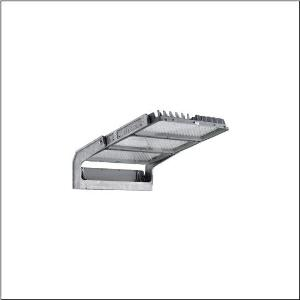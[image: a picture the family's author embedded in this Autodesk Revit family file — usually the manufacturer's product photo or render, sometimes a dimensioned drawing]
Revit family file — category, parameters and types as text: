
# Revit family: floodlight_fl_11_maxi_pro___rs08_5xa779224l01gb_ce58
name_source: partatom
category: Lighting Fixtures
units: mm (PartAtom-declared; Revit-internal decimal feet)

## family parameters
Cut with Voids When Loaded = No
Host = Face
Light Source = No
Part Type = Normal
Room Calculation Point = No
Round Connector Dimension = Use Diameter
Shared = No

## types (1)
- --- (1 x LED, 121700 lm, 1227.1 W, 5700K)
    Apparent Load = 1227 VA
    CIE Flux Codes = 70 87 98 100 100
    Color Rendering = 90
    Color Temperature = 5700K
    Default Elevation = 1800 mm
    Description = Floodlight FL 11  maxi  pro floodlight; light control with lens of PMMA; cover panel of toughened safety glass, transparent; light distribution: RS08, rotationally symmetric direct distribution, LED; colour temperature: 5700K, rated luminous flux: 121.700lm, colour rendering: CRI > 90, light colour: 957; luminous efficacy: 99lm/W; brightness control: DMX+RDM; with terminal, 6-pole, max. 2.5mm², mains connection: 220..240V/380..400V AC, 50/60Hz, surge voltage resistance: line to ground: 10kV, LED service life up to 100,000h L90. Typical operating time: 1000h per year., ECG replaceable separately, LED unit replaceable without ESD environment, dustproof LED module, dimming range 10..100%; 1227W floodlight with 3x LED unit of diecast aluminium, coated grey; length: 1.003mm / width: 651mm / height: 338mm; mounting bracket, of diecast aluminium, uncoated, natural, equipment: Power, protection rating (complete): IP66; insulation class (complete): insulation class I (protective earthing); certification: CE, ENEC, VDE; ball protection: ball impact resistant, only for outdoor installations in the designated locations, permissible operating ambient temperature: -45..+55°C, permissible storage temperature: -40..+85°Cpackaging unit: 1 piece

Light Distribution: RS08
    Height = 320 mm
    Lamp = 1 x LED
    Lamp Light Flux = 121700 lm
    Lamp Power = 1227.1 W
    Lamp count = 1
    Length = 1002 mm
    Luminous efficacy = 99 lm/W
    Manufacturer = Siteco
    ModVariant = No
    Model = 5XA779224L01GB
    Mounting Place = Ceiling
    Mounting Type = Surface mounted
    Number of Poles = 1
    OnlyDefault = Yes
    Power Factor = 1
    Product Name = Floodlight FL 11 maxi pro | RS08
    Product group = floodlight | ceiling mounted
    ProductGroupID = 303
    Protection Class = Protection class I
    Protection Degree = IP 66
    RLX_Detail_Level = 1
    RLX_Emergency_Light_Flux = 0 lm
    RLX_Emergency_Type = 0
    RLX_Emergency_Type_DB = No
    RlxData = <blob elided: 40189 chars, md5=37dddfd6>
    Socket = socket
    Standby Power = 0 W
    System Light Flux = 121700 lm
    System Power = 1227 W
    Type Comments = factory setting: luminous flux: 100 % | dim-lin: 255 | 840 mA
    Type Image = l_1356210.jpg
    URL = http://relux.com
    VarID = @adj_033761
    Voltage = 0 V
    Weight = 0.00 kg
    Width = 655 mm

## geometry (parser evidence)
native form markers: Blend x4, Sweep x12
no freeform markers — native parametric forms only
